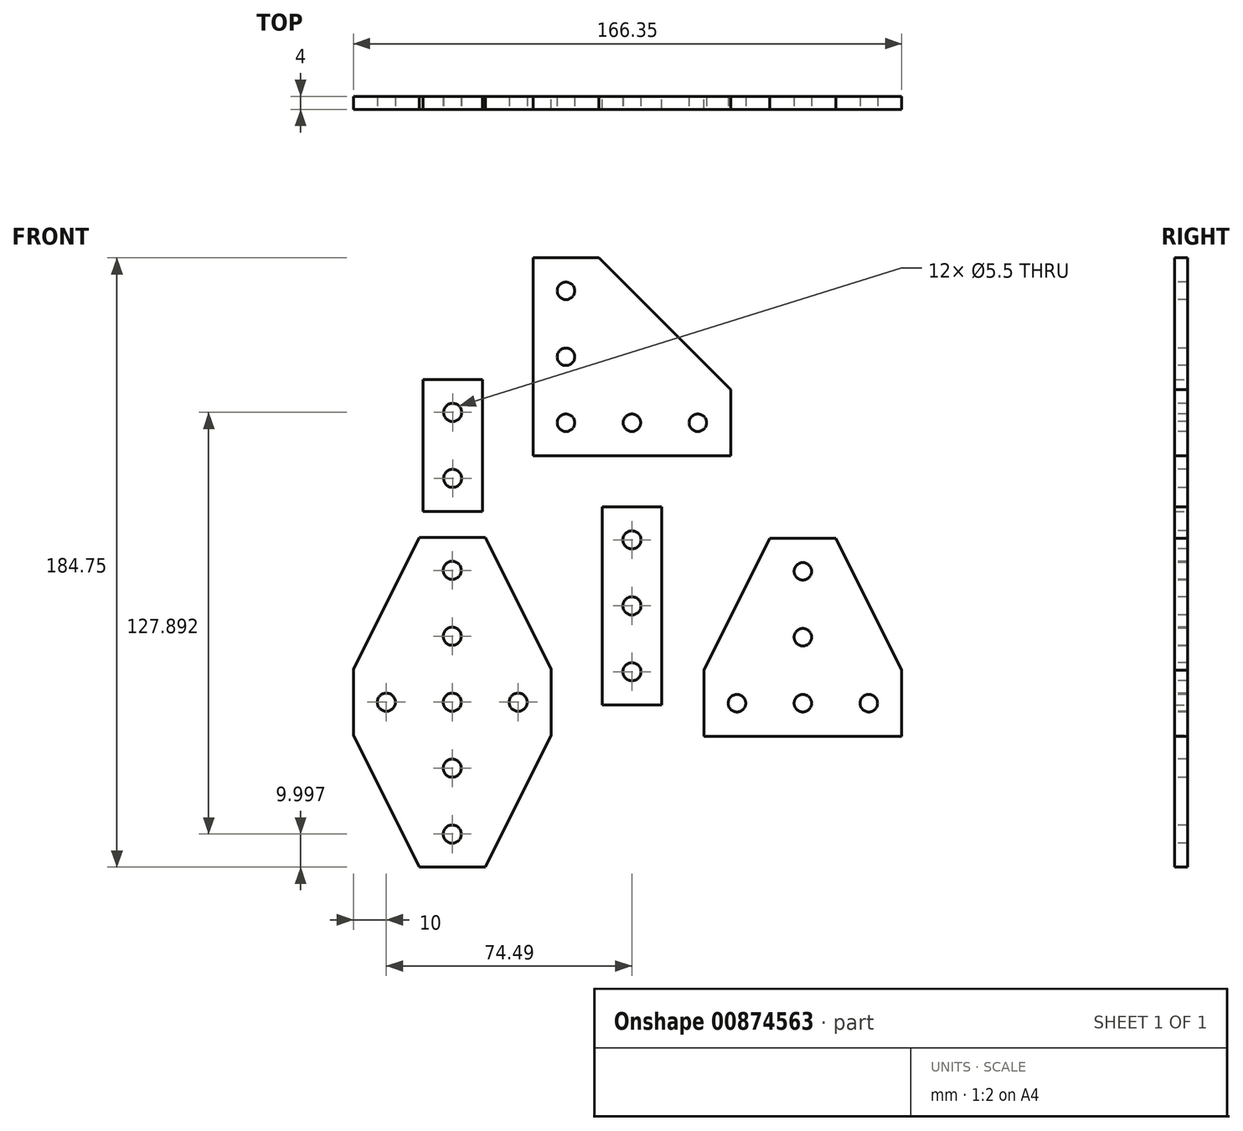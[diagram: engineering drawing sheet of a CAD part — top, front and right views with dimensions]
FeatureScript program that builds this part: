
annotation { "Feature Type Name" : "Feature", "Feature Type Description" : "" }
export const myFeature = defineFeature(function(context is Context, id is Id, definition is map)
    precondition{}
    {
        {
            var Q0;
            Q0=qCreatedBy(makeId("Front.planeOp"),FACE);
            var sketch = newSketch(context, id + "F0", { "sketchPlane" : qUnion([Q0])});
            skLineSegment(sketch, "E0.bottom", {"start": v(-30, 45.52) * mm, "end": v(30, 45.52) * mm});
            skLineSegment(sketch, "E0.top", {"start": v(-30, 105.52) * mm, "end": v(-10, 105.52) * mm});
            skLineSegment(sketch, "E0.left", {"start": v(-30, 45.52) * mm, "end": v(-30, 105.52) * mm});
            skLineSegment(sketch, "E0.right", {"start": v(30, 45.52) * mm, "end": v(30, 65.52) * mm});
            skPoint(sketch, "E0.middle", {"position": v(0, 75.52) * mm});
            skLineSegment(sketch, "E1", {"start": v(-10, 105.52) * mm, "end": v(30, 65.52) * mm});
            skPoint(sketch, "E2", {"position": v(-20, 55.52) * mm});
            skPoint(sketch, "E3", {"position": v(-20, 75.52) * mm});
            skPoint(sketch, "E4", {"position": v(-20, 95.52) * mm});
            skPoint(sketch, "E5", {"position": v(0, 55.52) * mm});
            skPoint(sketch, "E6", {"position": v(20, 55.52) * mm});
            skPoint(sketch, "E7.orphan", {"position": v(30, 105.52) * mm});
            skSolve(sketch);
        }
        {
            var Q0;
            Q0=makeQuery(id+"F0.imprint","IMPRINT",FACE,{"disambiguationData":[TD([[makeQuery(id+"F0.imprint","IMPRINT",EDGE,{"derivedFrom":sQuery(id+"F0.wireOp",EDGE,"E0.bottom")}),1.0]])]});
            extrude(context, id + "F1", {"entities" : qUnion([Q0]), "depth" : 4 * mm, "offsetDistance" : 25 * mm});
        }
        {
            var Q0;
            Q0=sQuery(id+"F0.wireOp",VERTEX,"E4");
            var Q1;
            Q1=sQuery(id+"F0.wireOp",VERTEX,"E3");
            var Q2;
            Q2=sQuery(id+"F0.wireOp",VERTEX,"E2");
            var Q3;
            Q3=sQuery(id+"F0.wireOp",VERTEX,"E5");
            var Q4;
            Q4=sQuery(id+"F0.wireOp",VERTEX,"E6");
            var Q5;
            Q5=makeQuery(id+"F1.opExtrude","SWEPT_BODY",BODY,{"disambiguationData":[OSD([sQuery(id+"F0.wireOp",EDGE,"E0.bottom"),sQuery(id+"F0.wireOp",EDGE,"E0.top"),sQuery(id+"F0.wireOp",EDGE,"E0.left"),sQuery(id+"F0.wireOp",EDGE,"E0.right"),sQuery(id+"F0.wireOp",EDGE,"E1")])]});
            hole(context, id + "F2", {"style" : HoleStyle.SIMPLE, "endStyle" : HoleEndStyle.BLIND, "oppositeDirection" : true, "holeDiameter" : 5.3 * mm, "majorDiameter" : 5 * mm, "holeDepth" : 12.7 * mm, "isTappedThrough" : true, "tappedDepth" : 9.53 * mm, "tapClearance" : 3, "locations" : qUnion([Q0, Q1, Q2, Q3, Q4]), "scope" : qUnion([Q5]), "startStyle" : HoleStartStyle.SKETCH});
        }
        {
            var Q0;
            Q0=qCreatedBy(makeId("Front.planeOp"),FACE);
            var sketch = newSketch(context, id + "F3", { "sketchPlane" : qUnion([Q0])});
            skLineSegment(sketch, "E8.bottom", {"start": v(21.86, -39.53) * mm, "end": v(81.86, -39.53) * mm});
            skLineSegment(sketch, "E8.left", {"start": v(21.86, -39.53) * mm, "end": v(21.86, -19.53) * mm});
            skLineSegment(sketch, "E8.right", {"start": v(81.86, -39.53) * mm, "end": v(81.86, -19.53) * mm});
            skPoint(sketch, "E8.middle", {"position": v(51.86, -29.53) * mm});
            skLineSegment(sketch, "E9.bottom", {"start": v(41.86, -39.53) * mm, "end": v(61.86, -39.53) * mm});
            skLineSegment(sketch, "E9.top", {"start": v(41.86, 20.47) * mm, "end": v(61.86, 20.47) * mm});
            skLineSegment(sketch, "E10", {"start": v(61.86, 20.47) * mm, "end": v(81.84, -19.53) * mm});
            skLineSegment(sketch, "E11", {"start": v(41.86, 20.47) * mm, "end": v(21.86, -19.53) * mm});
            skLineSegment(sketch, "E12.trimOffspring", {"start": v(81.84, -19.53) * mm, "end": v(81.86, -19.53) * mm});
            skPoint(sketch, "E13", {"position": v(51.86, -9.53) * mm});
            skPoint(sketch, "E14", {"position": v(51.86, 10.47) * mm});
            skPoint(sketch, "E15", {"position": v(71.86, -29.53) * mm});
            skPoint(sketch, "E16", {"position": v(31.86, -29.53) * mm});
            skSolve(sketch);
        }
        {
            var Q0;
            {var subQ1=sQuery(id+"F3.wireOp",EDGE,"E8.left");Q0=makeQuery(id+"F3.imprint","IMPRINT",FACE,{"disambiguationData":[TD([[makeQuery(id+"F3.imprint","IMPRINT",EDGE,{"derivedFrom":subQ1}),-1.0]])]});}
            extrude(context, id + "F4", {"entities" : qUnion([Q0]), "depth" : 4 * mm, "offsetDistance" : 25 * mm});
        }
        {
            var Q0;
            Q0=sQuery(id+"F3.wireOp",VERTEX,"E8.middle");
            var Q1;
            Q1=sQuery(id+"F3.wireOp",VERTEX,"E16");
            var Q2;
            Q2=sQuery(id+"F3.wireOp",VERTEX,"E15");
            var Q3;
            Q3=sQuery(id+"F3.wireOp",VERTEX,"E13");
            var Q4;
            Q4=sQuery(id+"F3.wireOp",VERTEX,"E14");
            var Q5;
            Q5=makeQuery(id+"F4.opExtrude","SWEPT_BODY",BODY,{"disambiguationData":[OSD([sQuery(id+"F3.wireOp",EDGE,"E8.bottom"),sQuery(id+"F3.wireOp",EDGE,"E8.left"),sQuery(id+"F3.wireOp",EDGE,"E8.right"),sQuery(id+"F3.wireOp",EDGE,"E9.bottom"),sQuery(id+"F3.wireOp",EDGE,"E9.top"),sQuery(id+"F3.wireOp",EDGE,"E10"),sQuery(id+"F3.wireOp",EDGE,"E11"),sQuery(id+"F3.wireOp",EDGE,"E12.trimOffspring")])]});
            hole(context, id + "F5", {"style" : HoleStyle.SIMPLE, "endStyle" : HoleEndStyle.BLIND, "oppositeDirection" : true, "holeDiameter" : 5.3 * mm, "majorDiameter" : 5 * mm, "holeDepth" : 12.7 * mm, "isTappedThrough" : true, "tappedDepth" : 9.53 * mm, "tapClearance" : 3, "locations" : qUnion([Q0, Q1, Q2, Q3, Q4]), "scope" : qUnion([Q5]), "startStyle" : HoleStartStyle.SKETCH});
        }
        {
            var Q0;
            Q0=qCreatedBy(makeId("Front.planeOp"),FACE);
            var sketch = newSketch(context, id + "F6", { "sketchPlane" : qUnion([Q0])});
            skLineSegment(sketch, "E17.bottom", {"start": v(-44.49, -79.23) * mm, "end": v(-64.49, -79.23) * mm});
            skLineSegment(sketch, "E17.top", {"start": v(-44.49, 20.77) * mm, "end": v(-64.49, 20.77) * mm});
            skLineSegment(sketch, "E18.left", {"start": v(-84.49, -39.23) * mm, "end": v(-84.49, -19.23) * mm});
            skLineSegment(sketch, "E18.right", {"start": v(-24.49, -39.23) * mm, "end": v(-24.49, -19.23) * mm});
            skPoint(sketch, "E18.middle", {"position": v(-54.49, -29.23) * mm});
            skLineSegment(sketch, "E19", {"start": v(-24.49, -19.23) * mm, "end": v(-44.49, 20.77) * mm});
            skLineSegment(sketch, "E20", {"start": v(-64.49, 20.77) * mm, "end": v(-84.49, -19.23) * mm});
            skLineSegment(sketch, "E21", {"start": v(-84.49, -39.23) * mm, "end": v(-64.49, -79.23) * mm});
            skLineSegment(sketch, "E22", {"start": v(-44.49, -79.23) * mm, "end": v(-24.49, -39.23) * mm});
            skPoint(sketch, "E23", {"position": v(-34.49, -29.23) * mm});
            skPoint(sketch, "E24", {"position": v(-54.49, -69.23) * mm});
            skPoint(sketch, "E25.0.1.0", {"position": v(-54.49, -49.23) * mm});
            skPoint(sketch, "E25.0.3.0", {"position": v(-54.49, -9.23) * mm});
            skPoint(sketch, "E25.0.4.0", {"position": v(-54.49, 10.77) * mm});
            skLineSegment(sketch, "E25.direction1", {"start": v(-54.49, -69.23) * mm, "end": v(-54.49, -69.23) * mm});
            skLineSegment(sketch, "E25.direction2", {"start": v(-54.49, -69.23) * mm, "end": v(-54.49, -49.23) * mm, "construction": true});
            skPoint(sketch, "E26.2.0.0", {"position": v(-74.49, -29.23) * mm});
            skLineSegment(sketch, "E26.direction1", {"start": v(-34.49, -29.23) * mm, "end": v(-54.49, -29.23) * mm, "construction": true});
            skSolve(sketch);
        }
        {
            var Q0;
            Q0=makeQuery(id+"F6.imprint","IMPRINT",FACE,{"disambiguationData":[TD([[makeQuery(id+"F6.imprint","IMPRINT",EDGE,{"derivedFrom":sQuery(id+"F6.wireOp",EDGE,"E17.bottom")}),-1.0]])]});
            extrude(context, id + "F7", {"entities" : qUnion([Q0]), "depth" : 4 * mm, "offsetDistance" : 25 * mm});
        }
        {
            var Q0;
            Q0=sQuery(id+"F6.wireOp",VERTEX,"E24");
            var Q1;
            Q1=sQuery(id+"F6.wireOp",VERTEX,"E25.0.1.0");
            var Q2;
            Q2=sQuery(id+"F6.wireOp",VERTEX,"E26.2.0.0");
            var Q3;
            Q3=sQuery(id+"F6.wireOp",VERTEX,"E18.middle");
            var Q4;
            Q4=sQuery(id+"F6.wireOp",VERTEX,"E23");
            var Q5;
            Q5=sQuery(id+"F6.wireOp",VERTEX,"E25.0.3.0");
            var Q6;
            Q6=sQuery(id+"F6.wireOp",VERTEX,"E25.0.4.0");
            var Q7;
            Q7=makeQuery(id+"F7.opExtrude","SWEPT_BODY",BODY,{"disambiguationData":[OSD([sQuery(id+"F6.wireOp",EDGE,"E17.bottom"),sQuery(id+"F6.wireOp",EDGE,"E17.top"),sQuery(id+"F6.wireOp",EDGE,"E18.left"),sQuery(id+"F6.wireOp",EDGE,"E18.right"),sQuery(id+"F6.wireOp",EDGE,"E19"),sQuery(id+"F6.wireOp",EDGE,"E20"),sQuery(id+"F6.wireOp",EDGE,"E21"),sQuery(id+"F6.wireOp",EDGE,"E22")])]});
            hole(context, id + "F8", {"style" : HoleStyle.SIMPLE, "endStyle" : HoleEndStyle.BLIND, "oppositeDirection" : true, "standardTappedOrClearance" : lookupTablePath({ "fit" : "Normal", "standard" : "ISO", "size" : "M5", "type" : "Clearance" }), "standardBlindInLast" : lookupTablePath({ "fit" : "Normal", "standard" : "ISO", "size" : "M5", "type" : "Clearance" }), "holeDiameter" : 5.5 * mm, "majorDiameter" : 5 * mm, "holeDepth" : 12.7 * mm, "isTappedThrough" : true, "tappedDepth" : 9.53 * mm, "tapClearance" : 3, "locations" : qUnion([Q0, Q1, Q2, Q3, Q4, Q5, Q6]), "scope" : qUnion([Q7]), "startStyle" : HoleStartStyle.SKETCH});
        }
        {
            var Q0;
            Q0=qCreatedBy(makeId("Front.planeOp"),FACE);
            var sketch = newSketch(context, id + "F9", { "sketchPlane" : qUnion([Q0])});
            skLineSegment(sketch, "E27.bottom", {"start": v(-63.36, 68.66) * mm, "end": v(-45.36, 68.66) * mm});
            skLineSegment(sketch, "E27.top", {"start": v(-63.36, 28.66) * mm, "end": v(-45.36, 28.66) * mm});
            skLineSegment(sketch, "E27.left", {"start": v(-63.36, 68.66) * mm, "end": v(-63.36, 28.66) * mm});
            skLineSegment(sketch, "E27.right", {"start": v(-45.36, 68.66) * mm, "end": v(-45.36, 28.66) * mm});
            skPoint(sketch, "E27.middle", {"position": v(-54.36, 48.66) * mm});
            skPoint(sketch, "E28", {"position": v(-54.36, 58.66) * mm});
            skPoint(sketch, "E29", {"position": v(-54.36, 38.66) * mm});
            skSolve(sketch);
        }
        {
            var Q0;
            Q0 = qSketchRegion(id + "F9", true);
            extrude(context, id + "F10", {"entities" : qUnion([Q0]), "depth" : 4 * mm, "offsetDistance" : 25 * mm});
        }
        {
            var Q0;
            Q0=sQuery(id+"F9.wireOp",VERTEX,"E28");
            var Q1;
            Q1=sQuery(id+"F9.wireOp",VERTEX,"E29");
            var Q2;
            Q2=makeQuery(id+"F10.opExtrude","SWEPT_BODY",BODY,{"disambiguationData":[OSD([sQuery(id+"F9.wireOp",EDGE,"E27.bottom"),sQuery(id+"F9.wireOp",EDGE,"E27.top"),sQuery(id+"F9.wireOp",EDGE,"E27.left"),sQuery(id+"F9.wireOp",EDGE,"E27.right")])]});
            hole(context, id + "F11", {"style" : HoleStyle.SIMPLE, "endStyle" : HoleEndStyle.BLIND, "oppositeDirection" : true, "standardTappedOrClearance" : lookupTablePath({ "fit" : "Normal", "standard" : "ISO", "size" : "M5", "type" : "Clearance" }), "standardBlindInLast" : lookupTablePath({ "fit" : "Normal", "standard" : "ISO", "size" : "M5", "type" : "Clearance" }), "holeDiameter" : 5.5 * mm, "majorDiameter" : 5 * mm, "holeDepth" : 12.7 * mm, "isTappedThrough" : true, "tappedDepth" : 9.53 * mm, "tapClearance" : 3, "locations" : qUnion([Q0, Q1]), "scope" : qUnion([Q2]), "startStyle" : HoleStartStyle.SKETCH});
        }
        {
            var Q0;
            Q0=qCreatedBy(makeId("Front.planeOp"),FACE);
            var sketch = newSketch(context, id + "F12", { "sketchPlane" : qUnion([Q0])});
            skLineSegment(sketch, "E30.bottom", {"start": v(-9, 30) * mm, "end": v(9, 30) * mm});
            skLineSegment(sketch, "E30.top", {"start": v(-9, -30) * mm, "end": v(9, -30) * mm});
            skLineSegment(sketch, "E30.left", {"start": v(-9, 30) * mm, "end": v(-9, -30) * mm});
            skLineSegment(sketch, "E30.right", {"start": v(9, 30) * mm, "end": v(9, -30) * mm});
            skPoint(sketch, "E30.middle", {"position": v(0, 0) * mm});
            skPoint(sketch, "E31", {"position": v(0, 20) * mm});
            skPoint(sketch, "E32", {"position": v(0, -20) * mm});
            skSolve(sketch);
        }
        {
            var Q0;
            Q0 = qSketchRegion(id + "F12", true);
            extrude(context, id + "F13", {"entities" : qUnion([Q0]), "depth" : 4 * mm, "offsetDistance" : 25 * mm});
        }
        {
            var Q0;
            Q0=sQuery(id+"F12.wireOp",VERTEX,"E31");
            var Q1;
            Q1=sQuery(id+"F12.wireOp",VERTEX,"E30.middle");
            var Q2;
            Q2=sQuery(id+"F12.wireOp",VERTEX,"E32");
            var Q3;
            Q3=makeQuery(id+"F13.opExtrude","SWEPT_BODY",BODY,{"disambiguationData":[OSD([sQuery(id+"F12.wireOp",EDGE,"E30.bottom"),sQuery(id+"F12.wireOp",EDGE,"E30.top"),sQuery(id+"F12.wireOp",EDGE,"E30.left"),sQuery(id+"F12.wireOp",EDGE,"E30.right")])]});
            hole(context, id + "F14", {"style" : HoleStyle.SIMPLE, "endStyle" : HoleEndStyle.BLIND, "oppositeDirection" : true, "standardTappedOrClearance" : lookupTablePath({ "fit" : "Normal", "standard" : "ISO", "size" : "M5", "type" : "Clearance" }), "standardBlindInLast" : lookupTablePath({ "fit" : "Normal", "standard" : "ISO", "size" : "M5", "type" : "Clearance" }), "holeDiameter" : 5.5 * mm, "majorDiameter" : 5 * mm, "holeDepth" : 12.7 * mm, "isTappedThrough" : true, "tappedDepth" : 9.53 * mm, "tapClearance" : 3, "locations" : qUnion([Q0, Q1, Q2]), "scope" : qUnion([Q3]), "startStyle" : HoleStartStyle.SKETCH});
        }
    });
